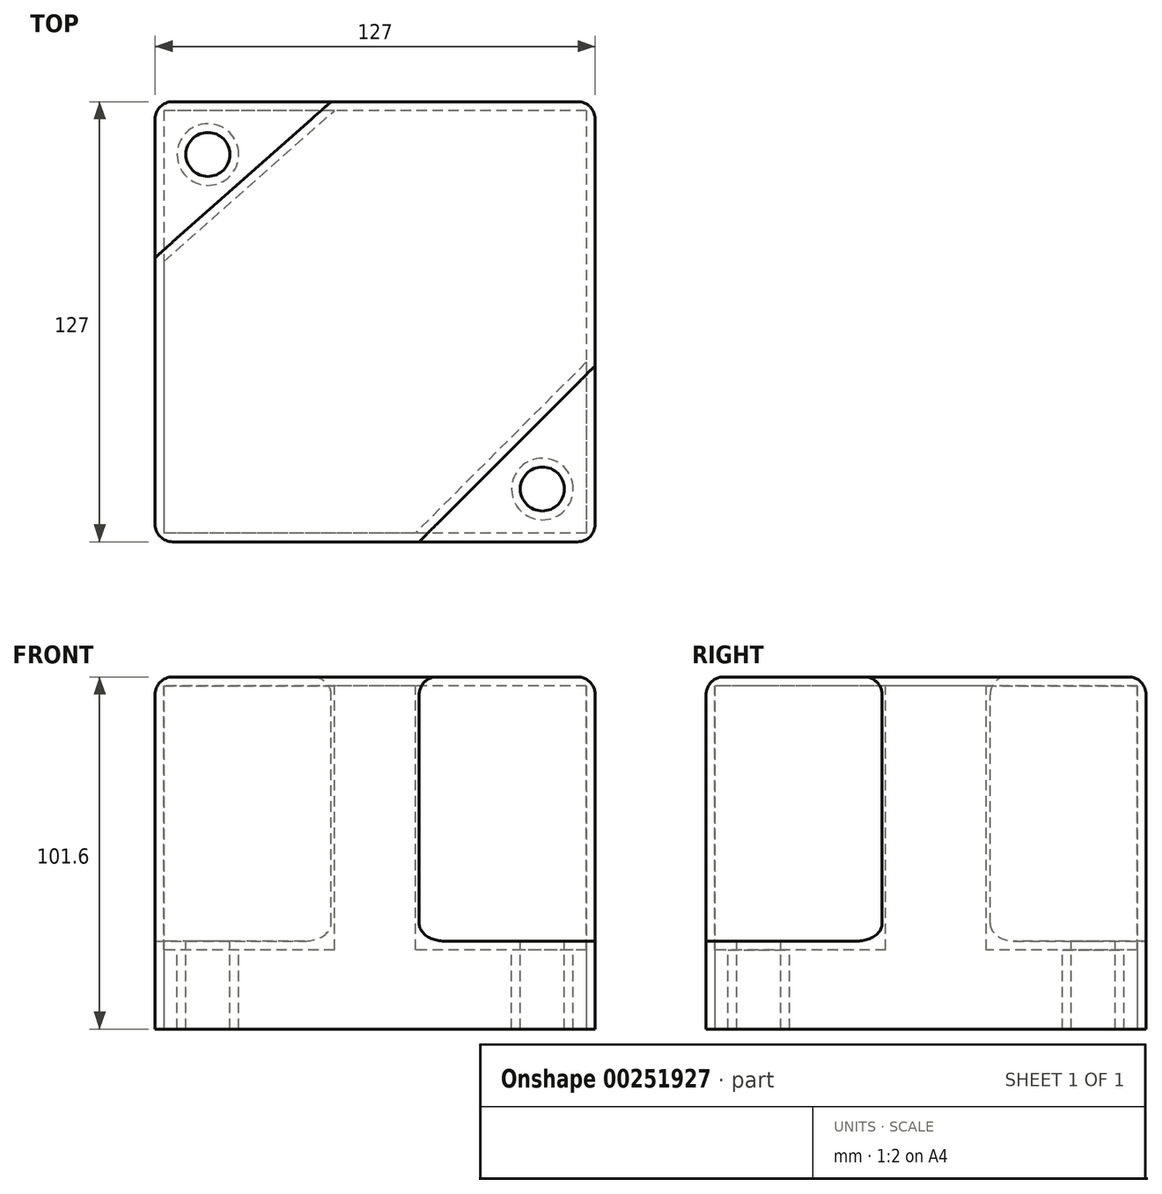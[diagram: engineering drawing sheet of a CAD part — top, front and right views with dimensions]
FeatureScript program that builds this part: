
annotation { "Feature Type Name" : "Feature", "Feature Type Description" : "" }
export const myFeature = defineFeature(function(context is Context, id is Id, definition is map)
    precondition{}
    {
        {
            var Q0;
            Q0=qCreatedBy(makeId("Top.planeOp"),FACE);
            var sketch = newSketch(context, id + "F0", { "sketchPlane" : qUnion([Q0])});
            skLineSegment(sketch, "E0.bottom", {"start": v(63.5, 63.5) * mm, "end": v(-63.5, 63.5) * mm});
            skLineSegment(sketch, "E0.top", {"start": v(63.5, -63.5) * mm, "end": v(-63.5, -63.5) * mm});
            skLineSegment(sketch, "E0.left", {"start": v(63.5, 63.5) * mm, "end": v(63.5, -63.5) * mm});
            skLineSegment(sketch, "E0.right", {"start": v(-63.5, 63.5) * mm, "end": v(-63.5, -63.5) * mm});
            skPoint(sketch, "E0.middle", {"position": v(0, 0) * mm});
            skSolve(sketch);
        }
        {
            var Q0;
            Q0=makeQuery(id+"F0.imprint","IMPRINT",FACE,{"disambiguationData":[TD([[makeQuery(id+"F0.imprint","IMPRINT",EDGE,{"derivedFrom":sQuery(id+"F0.wireOp",EDGE,"E0.bottom")}),1.0]])]});
            extrude(context, id + "F1", {"entities" : qUnion([Q0]), "depth" : 101.6 * mm});
        }
        {
            var Q0;
            Q0=makeQuery(id+"F1.opExtrude","CAP_FACE",FACE,{"disambiguationData":[OSD([sQuery(id+"F0.wireOp",EDGE,"E0.bottom"),sQuery(id+"F0.wireOp",EDGE,"E0.top"),sQuery(id+"F0.wireOp",EDGE,"E0.left"),sQuery(id+"F0.wireOp",EDGE,"E0.right")])],"isStart":false});
            var sketch = newSketch(context, id + "F2", { "sketchPlane" : qUnion([Q0])});
            skLineSegment(sketch, "E1", {"start": v(-63.5, 63.5) * mm, "end": v(-12.7, 63.5) * mm});
            skLineSegment(sketch, "E2", {"start": v(-63.5, 18.5) * mm, "end": v(-12.7, 63.5) * mm});
            skLineSegment(sketch, "E3", {"start": v(63.5, -63.5) * mm, "end": v(12.7, -63.5) * mm});
            skLineSegment(sketch, "E4", {"start": v(63.5, -63.5) * mm, "end": v(63.5, -12.7) * mm});
            skLineSegment(sketch, "E5", {"start": v(63.5, -12.7) * mm, "end": v(12.7, -63.5) * mm});
            skSolve(sketch);
        }
        {
            var Q0;
            {var subQ0=sQuery(id+"F2.wireOp",EDGE,"E1");Q0=makeQuery(id+"F2.imprint","IMPRINT",FACE,{"disambiguationData":[TD([[makeQuery(id+"F2.imprint","IMPRINT",EDGE,{"derivedFrom":subQ0}),1.0]])]});}
            var Q1;
            Q1=makeQuery(id+"F2.imprint","IMPRINT",FACE,{"disambiguationData":[TD([[makeQuery(id+"F2.imprint","IMPRINT",EDGE,{"derivedFrom":sQuery(id+"F2.wireOp",EDGE,"E3")}),-1.0]])]});
            extrude(context, id + "F3", {"entities" : qUnion([Q0, Q1]), "operationType" : NewBodyOperationType.REMOVE, "oppositeDirection" : true, "depth" : 76.2 * mm});
        }
        {
            var Q0;
            Q0=makeQuery(id+"F1.opExtrude","CAP_FACE",FACE,{"disambiguationData":[OSD([sQuery(id+"F0.wireOp",EDGE,"E0.bottom"),sQuery(id+"F0.wireOp",EDGE,"E0.top"),sQuery(id+"F0.wireOp",EDGE,"E0.left"),sQuery(id+"F0.wireOp",EDGE,"E0.right")])],"isStart":false});
            var sketch = newSketch(context, id + "F4", { "sketchPlane" : qUnion([Q0])});
            skCircle(sketch, "E6", {"center": v(-48.26, 48.26) * mm, "radius": 6.35 * mm});
            skCircle(sketch, "E7", {"center": v(48.26, -48.26) * mm, "radius": 6.35 * mm});
            skSolve(sketch);
        }
        {
            var Q0;
            Q0=makeQuery(id+"F4.imprint","IMPRINT",FACE,{"disambiguationData":[TD([[makeQuery(id+"F4.imprint","IMPRINT",EDGE,{"derivedFrom":sQuery(id+"F4.wireOp",EDGE,"E6")}),1.0]])]});
            var Q1;
            Q1=makeQuery(id+"F4.imprint","IMPRINT",FACE,{"disambiguationData":[TD([[makeQuery(id+"F4.imprint","IMPRINT",EDGE,{"derivedFrom":sQuery(id+"F4.wireOp",EDGE,"E7")}),1.0]])]});
            extrude(context, id + "F5", {"entities" : qUnion([Q0, Q1]), "operationType" : NewBodyOperationType.REMOVE, "oppositeDirection" : true, "depth" : 203.2 * mm});
        }
        {
            var Q0;
            Q0=makeQuery(id+"F1.opExtrude","CAP_FACE",FACE,{"disambiguationData":[OSD([sQuery(id+"F0.wireOp",EDGE,"E0.bottom"),sQuery(id+"F0.wireOp",EDGE,"E0.top"),sQuery(id+"F0.wireOp",EDGE,"E0.left"),sQuery(id+"F0.wireOp",EDGE,"E0.right")])],"isStart":true});
            shell(context, id + "F6", {"entities" : qUnion([Q0]), "thickness" : 2.54 * mm});
        }
        {
            var Q0;
            Q0=makeQuery(id+"F3.boolean.opBoolean","COPY",EDGE,{"derivedFrom":makeQuery(id+"F3.opExtrude","CAP_EDGE",EDGE,{"disambiguationData":[OSD([sQuery(id+"F2.wireOp",EDGE,"E5")])],"isStart":true})});
            var Q1;
            Q1=makeQuery(id+"F3.boolean.opBoolean","COPY",EDGE,{"derivedFrom":makeQuery(id+"F3.opExtrude","SWEPT_EDGE",EDGE,{"disambiguationData":[OSD([sQuery(id+"F0.wireOp",EDGE,"E0.top"),sQuery(id+"F2.wireOp",EDGE,"E3"),sQuery(id+"F2.wireOp",EDGE,"E5")])]})});
            var Q2;
            Q2=makeQuery(id+"F3.boolean.opBoolean","COPY",EDGE,{"derivedFrom":makeQuery(id+"F3.opExtrude","SWEPT_EDGE",EDGE,{"disambiguationData":[OSD([sQuery(id+"F0.wireOp",EDGE,"E0.left"),sQuery(id+"F2.wireOp",EDGE,"E4"),sQuery(id+"F2.wireOp",EDGE,"E5")])]})});
            var Q3;
            Q3=makeQuery(id+"F3.boolean.opBoolean","COPY",EDGE,{"derivedFrom":makeQuery(id+"F3.opExtrude","CAP_EDGE",EDGE,{"disambiguationData":[OSD([sQuery(id+"F2.wireOp",EDGE,"E4")])],"isStart":false})});
            var Q4;
            Q4=makeQuery(id+"F3.boolean.opBoolean","COPY",EDGE,{"derivedFrom":makeQuery(id+"F3.opExtrude","CAP_EDGE",EDGE,{"disambiguationData":[OSD([sQuery(id+"F2.wireOp",EDGE,"E3")])],"isStart":false})});
            var Q5;
            Q5=makeQuery(id+"F3.boolean.opBoolean","COPY",EDGE,{"derivedFrom":makeQuery(id+"F3.opExtrude","CAP_EDGE",EDGE,{"disambiguationData":[OSD([sQuery(id+"F2.wireOp",EDGE,"E5")])],"isStart":false})});
            var Q6;
            Q6=makeQuery(id+"F1.opExtrude","CAP_EDGE",EDGE,{"disambiguationData":[OSD([sQuery(id+"F0.wireOp",EDGE,"E0.left")])],"isStart":false});
            var Q7;
            Q7=makeQuery(id+"F1.opExtrude","CAP_EDGE",EDGE,{"disambiguationData":[OSD([sQuery(id+"F0.wireOp",EDGE,"E0.bottom")])],"isStart":false});
            var Q8;
            Q8=makeQuery(id+"F1.opExtrude","SWEPT_EDGE",EDGE,{"disambiguationData":[OSD([sQuery(id+"F0.wireOp",EDGE,"E0.bottom"),sQuery(id+"F0.wireOp",EDGE,"E0.left")])]});
            var Q9;
            Q9=makeQuery(id+"F3.boolean.opBoolean","COPY",EDGE,{"derivedFrom":makeQuery(id+"F3.opExtrude","CAP_EDGE",EDGE,{"disambiguationData":[OSD([sQuery(id+"F2.wireOp",EDGE,"E2")])],"isStart":true})});
            var Q10;
            Q10=makeQuery(id+"F3.boolean.opBoolean","COPY",EDGE,{"derivedFrom":makeQuery(id+"F3.opExtrude","SWEPT_EDGE",EDGE,{"disambiguationData":[OSD([sQuery(id+"F0.wireOp",EDGE,"E0.bottom"),sQuery(id+"F2.wireOp",EDGE,"E1"),sQuery(id+"F2.wireOp",EDGE,"E2")])]})});
            var Q11;
            Q11=makeQuery(id+"F3.boolean.opBoolean","COPY",EDGE,{"derivedFrom":makeQuery(id+"F3.opExtrude","CAP_EDGE",EDGE,{"disambiguationData":[OSD([sQuery(id+"F2.wireOp",EDGE,"E2")])],"isStart":false})});
            var Q12;
            Q12=makeQuery(id+"F3.boolean.opBoolean","COPY",EDGE,{"derivedFrom":makeQuery(id+"F3.opExtrude","CAP_EDGE",EDGE,{"disambiguationData":[OSD([sQuery(id+"F2.wireOp",EDGE,"E1")])],"isStart":false})});
            var Q13;
            Q13=makeQuery(id+"F3.boolean.opBoolean","COPY",EDGE,{"derivedFrom":makeQuery(id+"F3.opExtrude","CAP_EDGE",EDGE,{"disambiguationData":[OSD([sQuery(id+"F0.wireOp",EDGE,"E0.right")])],"isStart":false})});
            var Q14;
            Q14=makeQuery(id+"F3.boolean.opBoolean","COPY",EDGE,{"derivedFrom":makeQuery(id+"F3.opExtrude","SWEPT_EDGE",EDGE,{"disambiguationData":[OSD([sQuery(id+"F0.wireOp",EDGE,"E0.right"),sQuery(id+"F2.wireOp",EDGE,"E2")])]})});
            var Q15;
            Q15=makeQuery(id+"F1.opExtrude","CAP_EDGE",EDGE,{"disambiguationData":[OSD([sQuery(id+"F0.wireOp",EDGE,"E0.right")])],"isStart":false});
            var Q16;
            Q16=makeQuery(id+"F1.opExtrude","SWEPT_EDGE",EDGE,{"disambiguationData":[OSD([sQuery(id+"F0.wireOp",EDGE,"E0.bottom"),sQuery(id+"F0.wireOp",EDGE,"E0.right")])]});
            var Q17;
            Q17=makeQuery(id+"F1.opExtrude","SWEPT_EDGE",EDGE,{"disambiguationData":[OSD([sQuery(id+"F0.wireOp",EDGE,"E0.top"),sQuery(id+"F0.wireOp",EDGE,"E0.left")])]});
            var Q18;
            Q18=makeQuery(id+"F1.opExtrude","CAP_EDGE",EDGE,{"disambiguationData":[OSD([sQuery(id+"F0.wireOp",EDGE,"E0.top")])],"isStart":false});
            var Q19;
            Q19=makeQuery(id+"F1.opExtrude","SWEPT_EDGE",EDGE,{"disambiguationData":[OSD([sQuery(id+"F0.wireOp",EDGE,"E0.top"),sQuery(id+"F0.wireOp",EDGE,"E0.right")])]});
            fillet(context, id + "F7", {"entities" : qUnion([Q0, Q1, Q2, Q3, Q4, Q5, Q6, Q7, Q8, Q9, Q10, Q11, Q12, Q13, Q14, Q15, Q16, Q17, Q18, Q19]), "radius" : 5.08 * mm, "tangentPropagation" : true, "allowEdgeOverflow" : false});
        }
    });
